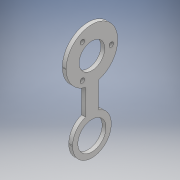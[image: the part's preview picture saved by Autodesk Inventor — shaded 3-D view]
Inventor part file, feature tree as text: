
AUTODESK INVENTOR PART (.ipt)
format: ipt  version: 2017 SP1 (Build 210196100, 196)  size: 335,872 bytes
history: native  units: mm
features: sketch x6, extrude x4, fillet x3, hole x2
ambient origin geometry x8: Origin, YZ Plane, XZ Plane, XY Plane, X Axis, Y Axis, Z Axis, Center Point
bodies: Solide1 (feature_tree)
feature tree (15):
  extrude  "Extrusion1"  Depth=65.0mm
  extrude  "Extrusion2"  Depth=10.0mm
  extrude  "Extrusion3"  Depth=5.0mm
  hole  "Perçage1"  [1 undecoded]
  fillet  "Congé1"  Radius=49.2442mm
  fillet  "Congé2"  Radius=5.0mm
  extrude  "Extrusion4"  Depth=3.0mm TaperAngle=0.0deg
  hole  "Perçage2"  [1 undecoded]
  fillet  "Congé3"  Radius=25.0mm
  sketch  "Esquisse1"
  sketch  "Esquisse2"
  sketch  "Esquisse3"
  sketch  "Esquisse4"
  sketch  "Esquisse5"
  sketch  "Esquisse6"
note: 2 required parameter values undecoded (feature->parameter linkage not recoverable at this tier; creation-order binding heuristic only, values carry confidence <= 0.55)
